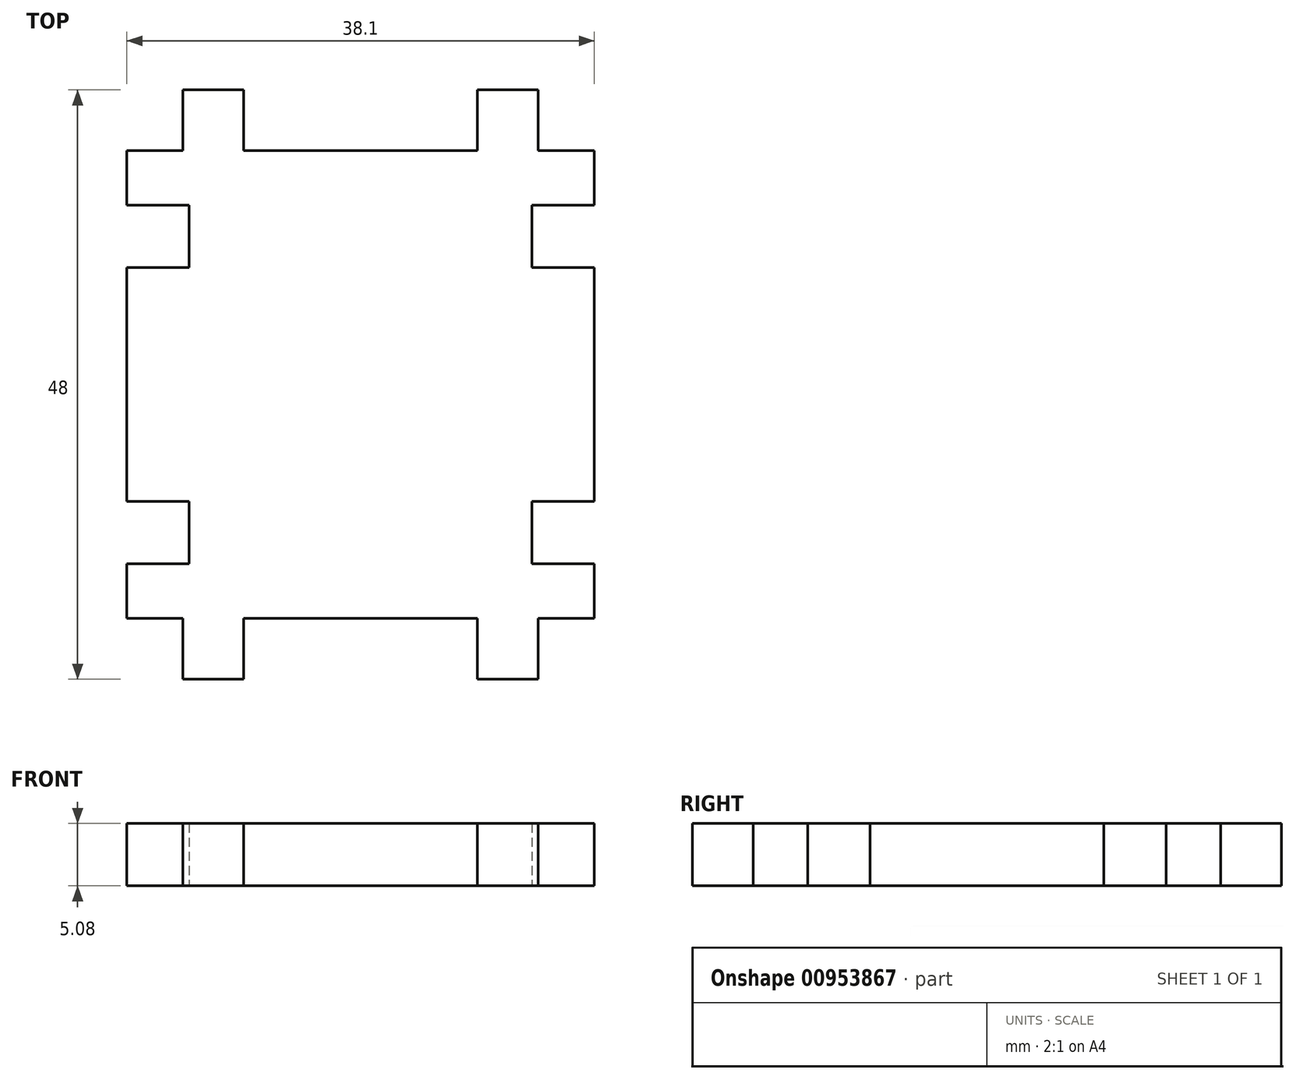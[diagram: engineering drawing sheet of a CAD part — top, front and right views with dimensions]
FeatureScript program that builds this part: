
annotation { "Feature Type Name" : "Feature", "Feature Type Description" : "" }
export const myFeature = defineFeature(function(context is Context, id is Id, definition is map)
    precondition{}
    {
        {
            var Q0;
            Q0=qCreatedBy(makeId("Top.planeOp"),FACE);
            var sketch = newSketch(context, id + "F0", { "sketchPlane" : qUnion([Q0])});
            skLineSegment(sketch, "E0.top", {"start": v(-19.05, -19.05) * mm, "end": v(19.05, -19.05) * mm});
            skLineSegment(sketch, "E0.right", {"start": v(19.05, 19.05) * mm, "end": v(19.05, -19.05) * mm});
            skPoint(sketch, "E0.middle", {"position": v(0, 0) * mm});
            skLineSegment(sketch, "E1", {"start": v(-19.05, 0) * mm, "end": v(19.05, 0) * mm});
            skLineSegment(sketch, "E2", {"start": v(0, 19.05) * mm, "end": v(0, -19.05) * mm});
            skLineSegment(sketch, "E3", {"start": v(-19.05, 19.05) * mm, "end": v(-19.05, 0) * mm});
            skLineSegment(sketch, "E4", {"start": v(-19.05, 0) * mm, "end": v(-19.05, -19.05) * mm});
            skLineSegment(sketch, "E5", {"start": v(-19.05, 9.53) * mm, "end": v(-13.97, 9.53) * mm});
            skLineSegment(sketch, "E6", {"start": v(-13.97, 9.53) * mm, "end": v(-13.97, 14.6) * mm});
            skLineSegment(sketch, "E7", {"start": v(-13.97, 14.6) * mm, "end": v(-19.05, 14.6) * mm});
            skLineSegment(sketch, "E8.MirrorCS", {"start": v(-19.05, -9.53) * mm, "end": v(-13.97, -9.53) * mm});
            skLineSegment(sketch, "E9.MirrorCS", {"start": v(-13.97, -9.53) * mm, "end": v(-13.97, -14.6) * mm});
            skLineSegment(sketch, "E10.MirrorCS", {"start": v(-13.97, -14.6) * mm, "end": v(-19.05, -14.6) * mm});
            skLineSegment(sketch, "E11.MirrorCS", {"start": v(13.97, 9.52) * mm, "end": v(13.97, 14.6) * mm});
            skLineSegment(sketch, "E12.MirrorCS", {"start": v(13.97, 14.6) * mm, "end": v(19.05, 14.6) * mm});
            skLineSegment(sketch, "E13.MirrorCS", {"start": v(19.05, 9.52) * mm, "end": v(13.97, 9.52) * mm});
            skLineSegment(sketch, "E14.MirrorCS", {"start": v(19.05, -9.53) * mm, "end": v(13.97, -9.53) * mm});
            skLineSegment(sketch, "E15.MirrorCS", {"start": v(13.97, -9.53) * mm, "end": v(13.97, -14.6) * mm});
            skLineSegment(sketch, "E16.MirrorCS", {"start": v(13.97, -14.6) * mm, "end": v(19.05, -14.6) * mm});
            skLineSegment(sketch, "E17", {"start": v(-19.05, 19.05) * mm, "end": v(0, 19.05) * mm});
            skLineSegment(sketch, "E18", {"start": v(0, 19.05) * mm, "end": v(19.05, 19.05) * mm});
            skLineSegment(sketch, "E19", {"start": v(-9.52, 19.05) * mm, "end": v(-9.52, 24) * mm});
            skLineSegment(sketch, "E20", {"start": v(-9.52, 24) * mm, "end": v(-14.48, 24) * mm});
            skLineSegment(sketch, "E21", {"start": v(-14.48, 24) * mm, "end": v(-14.48, 19.05) * mm});
            skLineSegment(sketch, "E22", {"start": v(9.53, 19.05) * mm, "end": v(9.53, 24) * mm});
            skLineSegment(sketch, "E23", {"start": v(9.53, 24) * mm, "end": v(14.48, 24) * mm});
            skLineSegment(sketch, "E24", {"start": v(14.48, 24) * mm, "end": v(14.48, 19.05) * mm});
            skLineSegment(sketch, "E25.MirrorCS", {"start": v(-9.52, -19.05) * mm, "end": v(-9.52, -24) * mm});
            skLineSegment(sketch, "E26.MirrorCS", {"start": v(-9.52, -24) * mm, "end": v(-14.48, -24) * mm});
            skLineSegment(sketch, "E27.MirrorCS", {"start": v(-14.48, -24) * mm, "end": v(-14.48, -19.05) * mm});
            skLineSegment(sketch, "E28.MirrorCS", {"start": v(9.53, -19.05) * mm, "end": v(9.53, -24) * mm});
            skLineSegment(sketch, "E29.MirrorCS", {"start": v(9.53, -24) * mm, "end": v(14.48, -24) * mm});
            skLineSegment(sketch, "E30.MirrorCS", {"start": v(14.48, -24) * mm, "end": v(14.48, -19.05) * mm});
            skSolve(sketch);
        }
        {
            var Q0;
            {var subQ9=sQuery(id+"F0.wireOp",EDGE,"E5");Q0=makeQuery(id+"F0.imprint","IMPRINT",FACE,{"disambiguationData":[TD([[makeQuery(id+"F0.imprint","IMPRINT",EDGE,{"derivedFrom":subQ9}),-1.0]])]});}
            var Q1;
            Q1=makeQuery(id+"F0.imprint","IMPRINT",FACE,{"disambiguationData":[TD([[makeQuery(id+"F0.imprint","IMPRINT",EDGE,{"derivedFrom":sQuery(id+"F0.wireOp",EDGE,"E11.MirrorCS")}),1.0]])]});
            var Q2;
            {var subQ8=sQuery(id+"F0.wireOp",EDGE,"E14.MirrorCS");Q2=makeQuery(id+"F0.imprint","IMPRINT",FACE,{"disambiguationData":[TD([[makeQuery(id+"F0.imprint","IMPRINT",EDGE,{"derivedFrom":subQ8}),-1.0]])]});}
            var Q3;
            {var subQ8=sQuery(id+"F0.wireOp",EDGE,"E8.MirrorCS");Q3=makeQuery(id+"F0.imprint","IMPRINT",FACE,{"disambiguationData":[TD([[makeQuery(id+"F0.imprint","IMPRINT",EDGE,{"derivedFrom":subQ8}),1.0]])]});}
            var Q4;
            {var subQ0=sQuery(id+"F0.wireOp",EDGE,"E19");Q4=makeQuery(id+"F0.imprint","IMPRINT",FACE,{"disambiguationData":[TD([[makeQuery(id+"F0.imprint","IMPRINT",EDGE,{"derivedFrom":subQ0}),1.0]])]});}
            var Q5;
            {var subQ0=sQuery(id+"F0.wireOp",EDGE,"E22");Q5=makeQuery(id+"F0.imprint","IMPRINT",FACE,{"disambiguationData":[TD([[makeQuery(id+"F0.imprint","IMPRINT",EDGE,{"derivedFrom":subQ0}),-1.0]])]});}
            var Q6;
            {var subQ0=sQuery(id+"F0.wireOp",EDGE,"E28.MirrorCS");Q6=makeQuery(id+"F0.imprint","IMPRINT",FACE,{"disambiguationData":[TD([[makeQuery(id+"F0.imprint","IMPRINT",EDGE,{"derivedFrom":subQ0}),1.0]])]});}
            var Q7;
            {var subQ0=sQuery(id+"F0.wireOp",EDGE,"E25.MirrorCS");Q7=makeQuery(id+"F0.imprint","IMPRINT",FACE,{"disambiguationData":[TD([[makeQuery(id+"F0.imprint","IMPRINT",EDGE,{"derivedFrom":subQ0}),-1.0]])]});}
            extrude(context, id + "F1", {"entities" : qUnion([Q0, Q1, Q2, Q3, Q4, Q5, Q6, Q7]), "depth" : 5.08 * mm, "offsetDistance" : 25.4 * mm});
        }
    });
